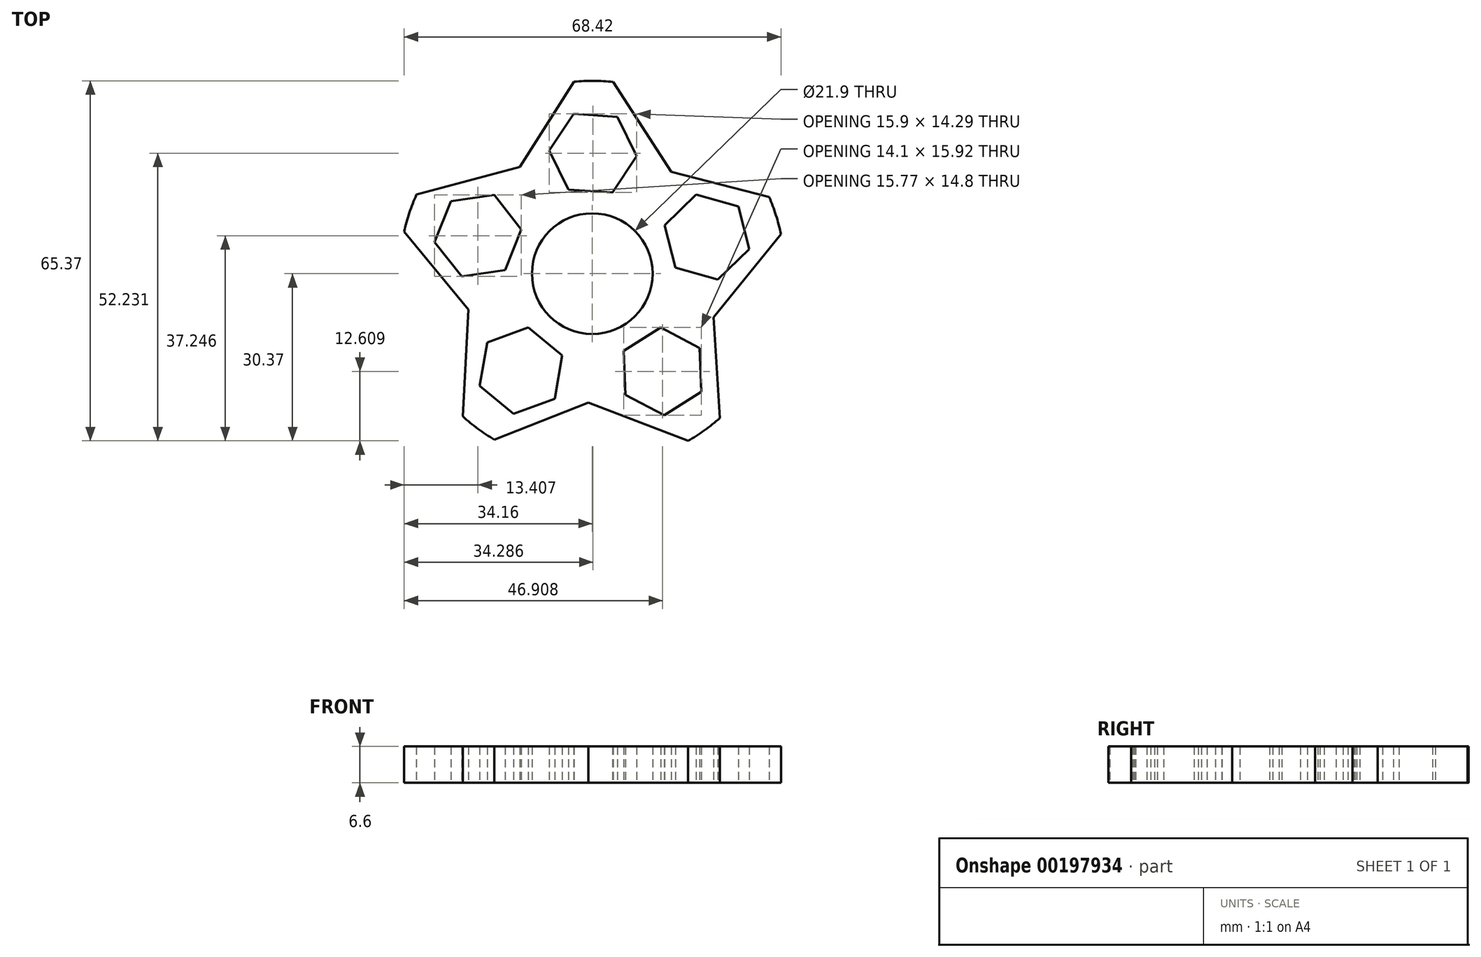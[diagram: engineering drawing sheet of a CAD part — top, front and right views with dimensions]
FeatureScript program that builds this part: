
annotation { "Feature Type Name" : "Feature", "Feature Type Description" : "" }
export const myFeature = defineFeature(function(context is Context, id is Id, definition is map)
    precondition{}
    {
        {
            var Q0;
            Q0=qCreatedBy(makeId("Top.planeOp"),FACE);
            var sketch = newSketch(context, id + "F0", { "sketchPlane" : qUnion([Q0])});
            skCircle(sketch, "E0", {"center": v(0, 0) * mm, "radius": 10.95 * mm});
            skArc(sketch, "E1", {"start": v(-23.51, -25.93) * mm, "mid": v(-20.76, -28.18) * mm, "end": v(-17.8, -30.14) * mm});
            skLineSegment(sketch, "E2.4.0", {"start": v(-25.6, 1.9) * mm, "end": v(-22.3, -0.32) * mm});
            skArc(sketch, "E3.trimOffspring", {"start": v(17.4, -30.37) * mm, "mid": v(20.38, -28.45) * mm, "end": v(23.16, -26.24) * mm});
            skArc(sketch, "E4.trimOffspring", {"start": v(34.26, 7.16) * mm, "mid": v(33.36, 10.6) * mm, "end": v(32.11, 13.92) * mm});
            skArc(sketch, "E5.trimOffspring", {"start": v(3.78, 34.8) * mm, "mid": v(0.23, 35) * mm, "end": v(-3.31, 34.84) * mm});
            skArc(sketch, "E6.trimOffspring", {"start": v(-31.92, 14.35) * mm, "mid": v(-33.21, 11.04) * mm, "end": v(-34.16, 7.61) * mm});
            skCircle(sketch, "E7.cCircle", {"center": v(-20.75, 6.88) * mm, "radius": 6.9 * mm, "construction": true});
            skLineSegment(sketch, "E7.0", {"start": v(-28.64, 5.73) * mm, "end": v(-25.68, 13.13) * mm});
            skLineSegment(sketch, "E7.1", {"start": v(-25.68, 13.13) * mm, "end": v(-17.8, 14.28) * mm});
            skLineSegment(sketch, "E7.2", {"start": v(-17.8, 14.28) * mm, "end": v(-12.87, 8.02) * mm});
            skLineSegment(sketch, "E7.3", {"start": v(-12.87, 8.02) * mm, "end": v(-15.82, 0.62) * mm});
            skLineSegment(sketch, "E7.4", {"start": v(-15.82, 0.62) * mm, "end": v(-23.7, -0.52) * mm});
            skLineSegment(sketch, "E7.5", {"start": v(-23.7, -0.52) * mm, "end": v(-28.64, 5.73) * mm});
            skPoint(sketch, "E7.0.midPoint", {"position": v(-27.16, 9.43) * mm});
            skPoint(sketch, "E8.orphan", {"position": v(-18.2, -3.07) * mm});
            skPoint(sketch, "E9.orphan", {"position": v(-15.34, -4.98) * mm});
            skPoint(sketch, "E10.orphan", {"position": v(-31.92, 14.35) * mm});
            skPoint(sketch, "E11.orphan", {"position": v(-9.48, 13.05) * mm});
            skPoint(sketch, "E12.orphan", {"position": v(3.78, 34.8) * mm});
            skPoint(sketch, "E13.orphan", {"position": v(8.58, 16.48) * mm});
            skPoint(sketch, "E14.end.orphan", {"position": v(0, -16.13) * mm});
            skLineSegment(sketch, "E15.1.0", {"start": v(-6.83, -22.7) * mm, "end": v(-14.3, -25.46) * mm});
            skLineSegment(sketch, "E15.1.1", {"start": v(-5.48, -14.86) * mm, "end": v(-6.83, -22.7) * mm});
            skLineSegment(sketch, "E15.1.2", {"start": v(-11.6, -9.76) * mm, "end": v(-5.48, -14.86) * mm});
            skLineSegment(sketch, "E15.1.3", {"start": v(-19.08, -12.52) * mm, "end": v(-11.6, -9.76) * mm});
            skLineSegment(sketch, "E15.1.4", {"start": v(-20.43, -20.37) * mm, "end": v(-19.08, -12.52) * mm});
            skLineSegment(sketch, "E15.1.5", {"start": v(-14.3, -25.46) * mm, "end": v(-20.43, -20.37) * mm});
            skLineSegment(sketch, "E15.2.0", {"start": v(19.49, -13.5) * mm, "end": v(19.8, -21.47) * mm});
            skLineSegment(sketch, "E15.2.1", {"start": v(12.44, -9.8) * mm, "end": v(19.49, -13.5) * mm});
            skLineSegment(sketch, "E15.2.2", {"start": v(5.7, -14.05) * mm, "end": v(12.44, -9.8) * mm});
            skLineSegment(sketch, "E15.2.3", {"start": v(6, -22.01) * mm, "end": v(5.7, -14.05) * mm});
            skLineSegment(sketch, "E15.2.4", {"start": v(13.06, -25.72) * mm, "end": v(6, -22.01) * mm});
            skLineSegment(sketch, "E15.2.5", {"start": v(19.8, -21.47) * mm, "end": v(13.06, -25.72) * mm});
            skLineSegment(sketch, "E15.3.0", {"start": v(18.87, 14.36) * mm, "end": v(26.54, 12.2) * mm});
            skLineSegment(sketch, "E15.3.1", {"start": v(13.16, 8.8) * mm, "end": v(18.87, 14.36) * mm});
            skLineSegment(sketch, "E15.3.2", {"start": v(15.12, 1.08) * mm, "end": v(13.16, 8.8) * mm});
            skLineSegment(sketch, "E15.3.3", {"start": v(22.8, -1.09) * mm, "end": v(15.12, 1.08) * mm});
            skLineSegment(sketch, "E15.3.4", {"start": v(28.5, 4.47) * mm, "end": v(22.8, -1.09) * mm});
            skLineSegment(sketch, "E15.3.5", {"start": v(26.54, 12.2) * mm, "end": v(28.5, 4.47) * mm});
            skLineSegment(sketch, "E15.4.0", {"start": v(-7.82, 22.38) * mm, "end": v(-3.4, 29) * mm});
            skLineSegment(sketch, "E15.4.1", {"start": v(-4.3, 15.24) * mm, "end": v(-7.82, 22.38) * mm});
            skLineSegment(sketch, "E15.4.2", {"start": v(3.65, 14.72) * mm, "end": v(-4.3, 15.24) * mm});
            skLineSegment(sketch, "E15.4.3", {"start": v(8.08, 21.34) * mm, "end": v(3.65, 14.72) * mm});
            skLineSegment(sketch, "E15.4.4", {"start": v(4.55, 28.49) * mm, "end": v(8.08, 21.34) * mm});
            skLineSegment(sketch, "E15.4.5", {"start": v(-3.4, 29) * mm, "end": v(4.55, 28.49) * mm});
            skLineSegment(sketch, "E16", {"start": v(-34.16, 7.61) * mm, "end": v(-22.48, -6.53) * mm});
            skPoint(sketch, "E16.endSnap0", {"position": v(-19.76, 0.05) * mm});
            skLineSegment(sketch, "E17", {"start": v(-23.51, -25.93) * mm, "end": v(-22.48, -6.53) * mm});
            skLineSegment(sketch, "E18.1.0", {"start": v(-17.8, -30.14) * mm, "end": v(-0.73, -23.4) * mm});
            skLineSegment(sketch, "E18.1.1", {"start": v(17.4, -30.37) * mm, "end": v(-0.73, -23.4) * mm});
            skLineSegment(sketch, "E18.2.0", {"start": v(23.16, -26.24) * mm, "end": v(22.03, -7.93) * mm});
            skLineSegment(sketch, "E18.2.1", {"start": v(34.26, 7.16) * mm, "end": v(22.03, -7.93) * mm});
            skLineSegment(sketch, "E18.3.0", {"start": v(32.11, 13.92) * mm, "end": v(14.35, 18.5) * mm});
            skLineSegment(sketch, "E18.3.1", {"start": v(3.78, 34.8) * mm, "end": v(14.35, 18.5) * mm});
            skLineSegment(sketch, "E18.4.0", {"start": v(-3.31, 34.84) * mm, "end": v(-13.16, 19.36) * mm});
            skLineSegment(sketch, "E18.4.1", {"start": v(-31.92, 14.35) * mm, "end": v(-13.16, 19.36) * mm});
            skPoint(sketch, "E19.orphan", {"position": v(-22.3, -3.14) * mm});
            skPoint(sketch, "E20.orphan", {"position": v(-19.76, -9.83) * mm});
            skPoint(sketch, "E21.orphan", {"position": v(3.24, -21.83) * mm});
            skPoint(sketch, "E22.orphan", {"position": v(-3.9, -22.18) * mm});
            skPoint(sketch, "E23.orphan", {"position": v(19.9, -10.57) * mm});
            skPoint(sketch, "E24.orphan", {"position": v(21.77, -3.67) * mm});
            skPoint(sketch, "E25.orphan", {"position": v(-9.88, 20.24) * mm});
            skPoint(sketch, "E26.orphan", {"position": v(-15.45, 15.76) * mm});
            skPoint(sketch, "E27.orphan", {"position": v(10.21, 19.57) * mm});
            skPoint(sketch, "E28.orphan", {"position": v(16.2, 15.65) * mm});
            skSolve(sketch);
        }
        {
            var Q0;
            Q0 = qSketchRegion(id + "F0", true);
            extrude(context, id + "F1", {"entities" : qUnion([Q0]), "depth" : 6.6 * mm, "offsetDistance" : 25 * mm});
        }
    });
